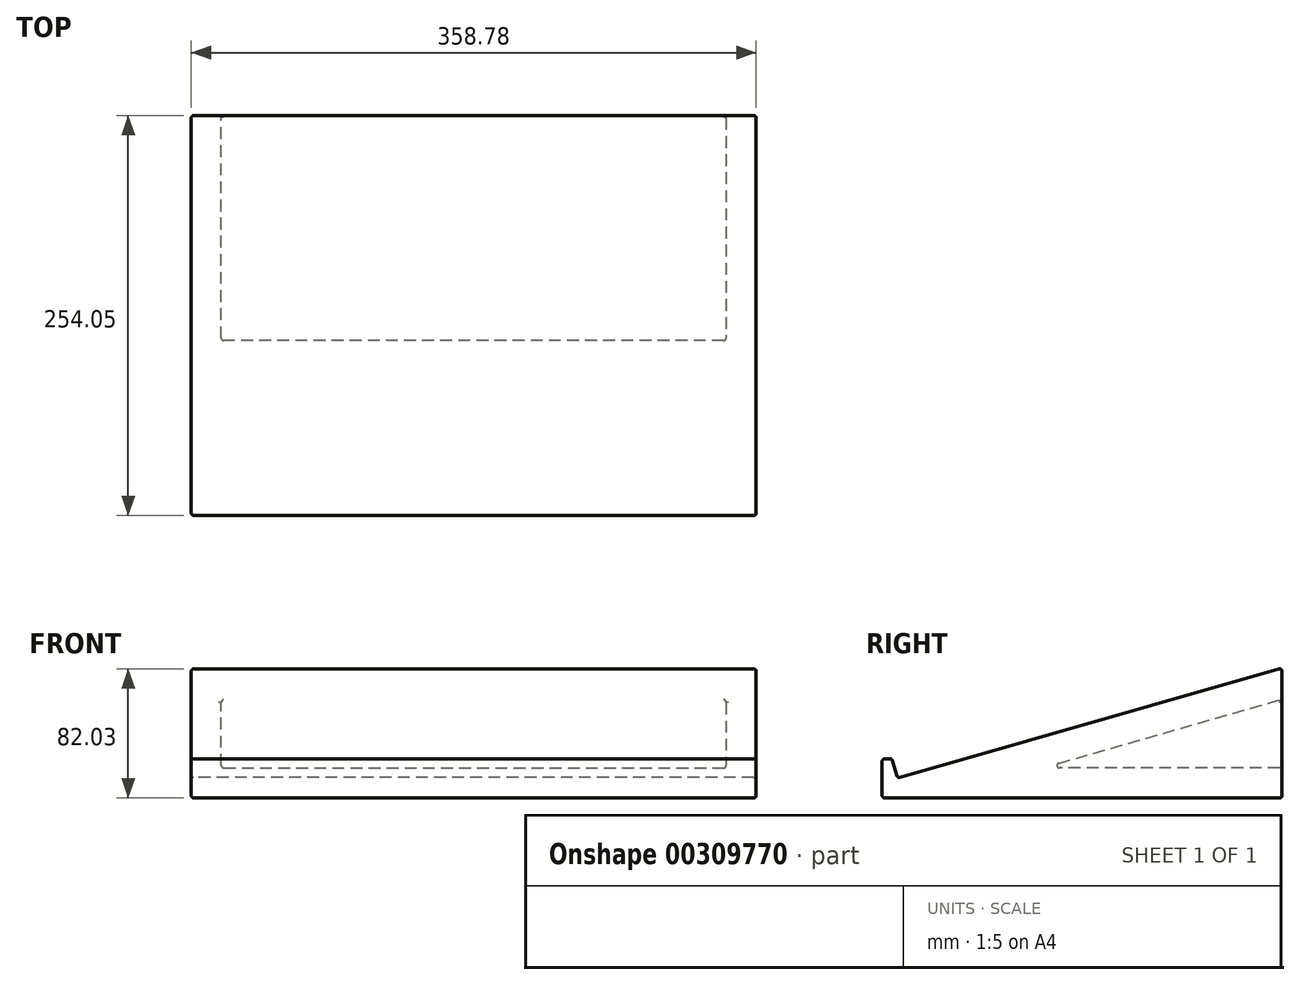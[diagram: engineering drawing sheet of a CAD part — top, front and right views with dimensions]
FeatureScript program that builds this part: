
annotation { "Feature Type Name" : "Feature", "Feature Type Description" : "" }
export const myFeature = defineFeature(function(context is Context, id is Id, definition is map)
    precondition{}
    {
        {
            var Q0;
            Q0=qCreatedBy(makeId("Right.planeOp"),FACE);
            var sketch = newSketch(context, id + "F0", { "sketchPlane" : qUnion([Q0])});
            skLineSegment(sketch, "E0", {"start": v(11.37, 13.14) * mm, "end": v(252.03, 81.97) * mm});
            skLineSegment(sketch, "E1", {"start": v(9.4, 14.23) * mm, "end": v(6.68, 23.76) * mm});
            skLineSegment(sketch, "E2", {"start": v(5.15, 24.91) * mm, "end": v(1.59, 24.91) * mm});
            skLineSegment(sketch, "E3", {"start": v(0, 23.32) * mm, "end": v(0, 1.59) * mm});
            skLineSegment(sketch, "E4", {"start": v(254.05, 80.44) * mm, "end": v(254.05, 1.59) * mm});
            skLineSegment(sketch, "E5", {"start": v(252.46, 0) * mm, "end": v(1.59, 0) * mm});
            skPoint(sketch, "E6.visualSharp", {"position": v(0, 24.91) * mm});
            skArc(sketch, "E6.filletArc", {"start": v(1.59, 24.91) * mm, "mid": v(0.46, 24.45) * mm, "end": v(0, 23.32) * mm});
            skPoint(sketch, "E7.visualSharp", {"position": v(6.35, 24.91) * mm});
            skArc(sketch, "E7.filletArc", {"start": v(6.68, 23.76) * mm, "mid": v(6.1, 24.6) * mm, "end": v(5.15, 24.91) * mm});
            skPoint(sketch, "E8.visualSharp", {"position": v(9.84, 12.7) * mm});
            skArc(sketch, "E8.filletArc", {"start": v(9.4, 14.23) * mm, "mid": v(10.16, 13.27) * mm, "end": v(11.37, 13.14) * mm});
            skPoint(sketch, "E9.visualSharp", {"position": v(0, 0) * mm});
            skArc(sketch, "E9.filletArc", {"start": v(0, 1.59) * mm, "mid": v(0.46, 0.46) * mm, "end": v(1.59, 0) * mm});
            skPoint(sketch, "E10.visualSharp", {"position": v(254.05, 82.55) * mm});
            skArc(sketch, "E10.filletArc", {"start": v(254.05, 80.44) * mm, "mid": v(253.42, 81.71) * mm, "end": v(252.03, 81.97) * mm});
            skPoint(sketch, "E11.visualSharp", {"position": v(254.05, 0) * mm});
            skArc(sketch, "E11.filletArc", {"start": v(252.46, 0) * mm, "mid": v(253.58, 0.46) * mm, "end": v(254.05, 1.59) * mm});
            skSolve(sketch);
        }
        {
            var Q0;
            Q0=makeQuery(id+"F0.imprint","IMPRINT",FACE,{"disambiguationData":[TD([[makeQuery(id+"F0.imprint","IMPRINT",EDGE,{"derivedFrom":sQuery(id+"F0.wireOp",EDGE,"E0")}),-1.0]])]});
            extrude(context, id + "F1", {"entities" : qUnion([Q0]), "endBound" : BoundingType.SYMMETRIC, "depth" : 358.77 * mm});
        }
        {
            var Q0;
            Q0=makeQuery(id+"F1.opExtrude","SWEPT_FACE",FACE,{"disambiguationData":[OSD([sQuery(id+"F0.wireOp",EDGE,"E4")])]});
            shell(context, id + "F2", {"entities" : qUnion([Q0]), "thickness" : 19.05 * mm});
        }
        {
            var Q0;
            Q0=makeQuery(id+"F1.opExtrude","CAP_EDGE",EDGE,{"disambiguationData":[OSD([sQuery(id+"F0.wireOp",EDGE,"E0")])],"isStart":true});
            var Q1;
            Q1=makeQuery(id+"F1.opExtrude","CAP_EDGE",EDGE,{"disambiguationData":[OSD([sQuery(id+"F0.wireOp",EDGE,"E0")])],"isStart":false});
            var Q2;
            {var subQ0=sQuery(id+"F0.wireOp",EDGE,"E4");Q2=makeQuery(id+"F2.opShell","OFFSET_EDGE",EDGE,{"disambiguationData":[OSD([subQ0]),TDD([makeQuery(id+"F1.opExtrude","CAP_EDGE",EDGE,{"disambiguationData":[OSD([subQ0])],"isStart":false})])]});}
            var Q3;
            Q3=makeQuery(id+"F2.opShell","OFFSET_EDGE",EDGE,{"disambiguationData":[OSD([sQuery(id+"F0.wireOp",EDGE,"E0"),sQuery(id+"F0.wireOp",EDGE,"E4"),sQuery(id+"F0.wireOp",EDGE,"E10.filletArc")])]});
            var Q4;
            {var subQ0=sQuery(id+"F0.wireOp",EDGE,"E4");Q4=makeQuery(id+"F2.opShell","OFFSET_EDGE",EDGE,{"disambiguationData":[OSD([subQ0]),TDD([makeQuery(id+"F1.opExtrude","CAP_EDGE",EDGE,{"disambiguationData":[OSD([subQ0])],"isStart":true})])]});}
            var Q5;
            Q5=makeQuery(id+"F2.opShell","OFFSET_EDGE",EDGE,{"disambiguationData":[OSD([sQuery(id+"F0.wireOp",EDGE,"E4"),sQuery(id+"F0.wireOp",EDGE,"E5"),sQuery(id+"F0.wireOp",EDGE,"E11.filletArc")])]});
            var Q6;
            Q6=makeQuery(id+"F2.opShell","TWEAK_EDGE",EDGE,{"derivedFrom":[makeQuery(id+"F1.opExtrude","SWEPT_FACE",FACE,{"disambiguationData":[OSD([sQuery(id+"F0.wireOp",EDGE,"E0")])]}),makeQuery(id+"F1.opExtrude","SWEPT_FACE",FACE,{"disambiguationData":[OSD([sQuery(id+"F0.wireOp",EDGE,"E5")])]})]});
            var Q7;
            {var subQ0=sQuery(id+"F0.wireOp",EDGE,"E0");Q7=makeQuery(id+"F2.opShell","OFFSET_EDGE",EDGE,{"disambiguationData":[OSD([subQ0]),TDD([makeQuery(id+"F1.opExtrude","CAP_EDGE",EDGE,{"disambiguationData":[OSD([subQ0])],"isStart":false})])]});}
            var Q8;
            {var subQ0=sQuery(id+"F0.wireOp",EDGE,"E5");Q8=makeQuery(id+"F2.opShell","OFFSET_EDGE",EDGE,{"disambiguationData":[OSD([subQ0]),TDD([makeQuery(id+"F1.opExtrude","CAP_EDGE",EDGE,{"disambiguationData":[OSD([subQ0])],"isStart":false})])]});}
            var Q9;
            {var subQ0=sQuery(id+"F0.wireOp",EDGE,"E0");Q9=makeQuery(id+"F2.opShell","OFFSET_EDGE",EDGE,{"disambiguationData":[OSD([subQ0]),TDD([makeQuery(id+"F1.opExtrude","CAP_EDGE",EDGE,{"disambiguationData":[OSD([subQ0])],"isStart":true})])]});}
            var Q10;
            {var subQ0=sQuery(id+"F0.wireOp",EDGE,"E5");Q10=makeQuery(id+"F2.opShell","OFFSET_EDGE",EDGE,{"disambiguationData":[OSD([subQ0]),TDD([makeQuery(id+"F1.opExtrude","CAP_EDGE",EDGE,{"disambiguationData":[OSD([subQ0])],"isStart":true})])]});}
            fillet(context, id + "F3", {"entities" : qUnion([Q0, Q1, Q2, Q3, Q4, Q5, Q6, Q7, Q8, Q9, Q10]), "radius" : 1.59 * mm, "tangentPropagation" : true, "allowEdgeOverflow" : false});
        }
    });
